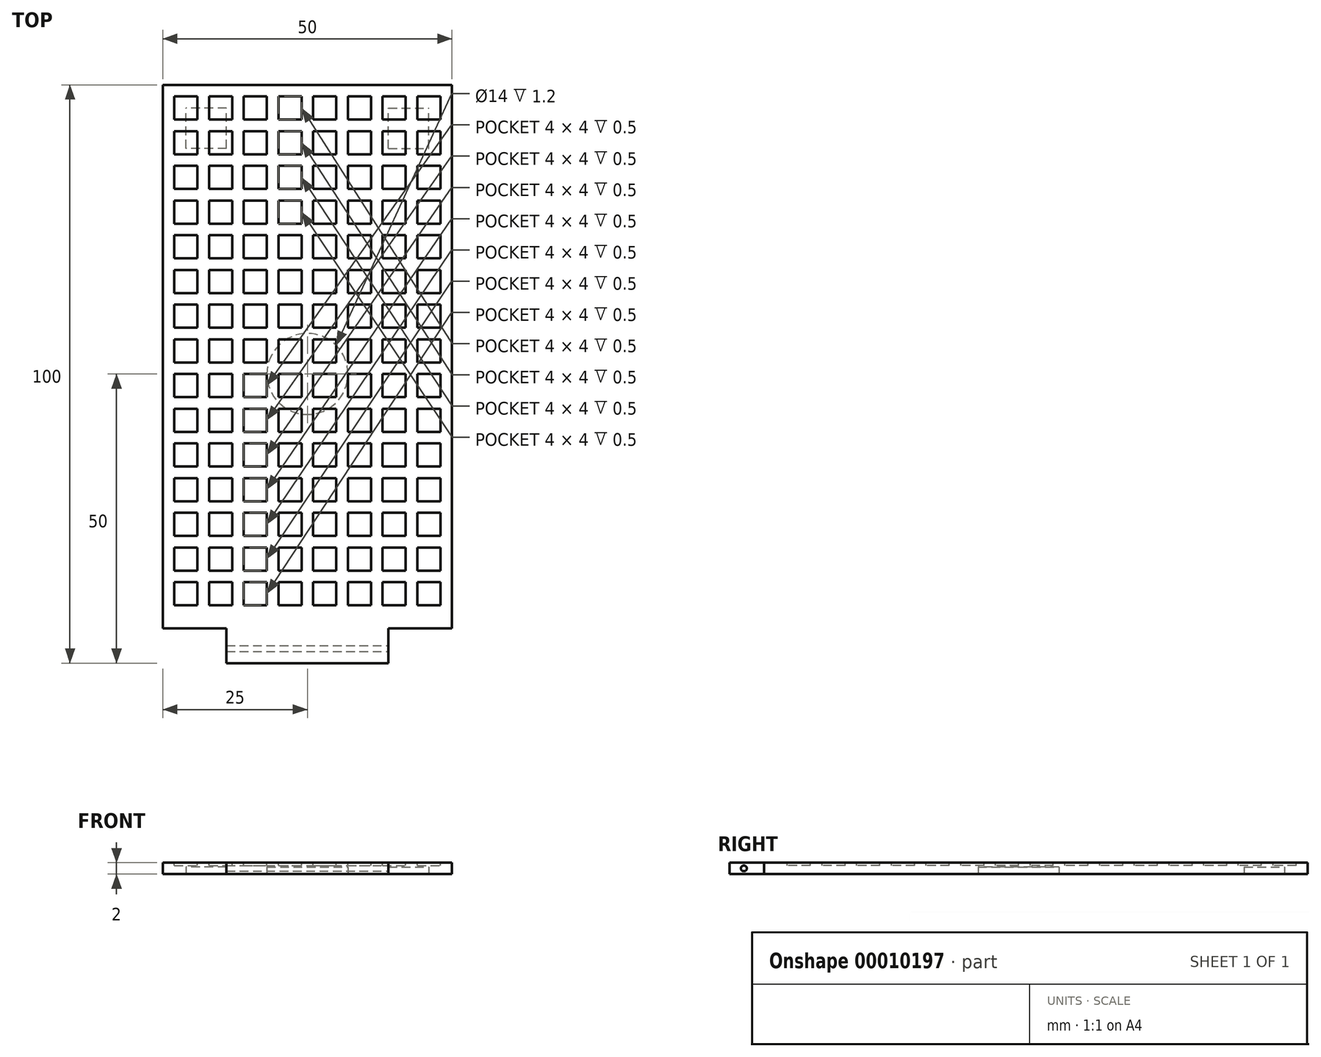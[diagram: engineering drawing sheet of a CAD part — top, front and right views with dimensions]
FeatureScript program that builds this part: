
annotation { "Feature Type Name" : "Feature", "Feature Type Description" : "" }
export const myFeature = defineFeature(function(context is Context, id is Id, definition is map)
    precondition{}
    {
        {
            var Q0;
            Q0=qCreatedBy(makeId("Top.planeOp"),FACE);
            var sketch = newSketch(context, id + "F0", { "sketchPlane" : qUnion([Q0])});
            skLineSegment(sketch, "E0.bottom", {"start": v(-28, -65.66) * mm, "end": v(0, -65.66) * mm});
            skLineSegment(sketch, "E0.top", {"start": v(-39, 34.34) * mm, "end": v(11, 34.34) * mm});
            skLineSegment(sketch, "E0.left", {"start": v(-39, -59.66) * mm, "end": v(-39, 34.34) * mm});
            skLineSegment(sketch, "E0.right", {"start": v(11, -59.66) * mm, "end": v(11, 34.34) * mm});
            skLineSegment(sketch, "E1.top", {"start": v(-39, -59.66) * mm, "end": v(-28, -59.66) * mm});
            skLineSegment(sketch, "E1.right", {"start": v(-28, -65.66) * mm, "end": v(-28, -59.66) * mm});
            skLineSegment(sketch, "E2.top", {"start": v(11, -59.66) * mm, "end": v(0, -59.66) * mm});
            skLineSegment(sketch, "E2.right", {"start": v(0, -65.66) * mm, "end": v(0, -59.66) * mm});
            skSolve(sketch);
        }
        {
            var Q0;
            Q0 = qSketchRegion(id + "F0", true);
            extrude(context, id + "F1", {"entities" : qUnion([Q0]), "depth" : 2 * mm});
        }
        {
            var Q0;
            Q0=makeQuery(id+"F1.opExtrude","CAP_FACE",FACE,{"disambiguationData":[OSD([sQuery(id+"F0.wireOp",EDGE,"E0.bottom"),sQuery(id+"F0.wireOp",EDGE,"E0.top"),sQuery(id+"F0.wireOp",EDGE,"E0.left"),sQuery(id+"F0.wireOp",EDGE,"E0.right"),sQuery(id+"F0.wireOp",EDGE,"E1.top"),sQuery(id+"F0.wireOp",EDGE,"E1.right"),sQuery(id+"F0.wireOp",EDGE,"E2.top"),sQuery(id+"F0.wireOp",EDGE,"E2.right")])],"isStart":false});
            var sketch = newSketch(context, id + "F2", { "sketchPlane" : qUnion([Q0])});
            skLineSegment(sketch, "E3.bottom", {"start": v(-37, 32.34) * mm, "end": v(-33, 32.34) * mm});
            skLineSegment(sketch, "E3.top", {"start": v(-37, 28.34) * mm, "end": v(-33, 28.34) * mm});
            skLineSegment(sketch, "E3.left", {"start": v(-37, 32.34) * mm, "end": v(-37, 28.34) * mm});
            skLineSegment(sketch, "E3.right", {"start": v(-33, 32.34) * mm, "end": v(-33, 28.34) * mm});
            skLineSegment(sketch, "E4.0.1.0", {"start": v(-37, 26.34) * mm, "end": v(-37, 22.34) * mm});
            skLineSegment(sketch, "E4.0.1.1", {"start": v(-33, 26.34) * mm, "end": v(-33, 22.34) * mm});
            skLineSegment(sketch, "E4.0.1.2", {"start": v(-37, 22.34) * mm, "end": v(-33, 22.34) * mm});
            skLineSegment(sketch, "E4.0.1.3", {"start": v(-37, 26.34) * mm, "end": v(-33, 26.34) * mm});
            skLineSegment(sketch, "E4.0.2.0", {"start": v(-37, 20.34) * mm, "end": v(-37, 16.34) * mm});
            skLineSegment(sketch, "E4.0.2.1", {"start": v(-33, 20.34) * mm, "end": v(-33, 16.34) * mm});
            skLineSegment(sketch, "E4.0.2.2", {"start": v(-37, 16.34) * mm, "end": v(-33, 16.34) * mm});
            skLineSegment(sketch, "E4.0.2.3", {"start": v(-37, 20.34) * mm, "end": v(-33, 20.34) * mm});
            skLineSegment(sketch, "E4.0.3.0", {"start": v(-37, 14.34) * mm, "end": v(-37, 10.34) * mm});
            skLineSegment(sketch, "E4.0.3.1", {"start": v(-33, 14.34) * mm, "end": v(-33, 10.34) * mm});
            skLineSegment(sketch, "E4.0.3.2", {"start": v(-37, 10.34) * mm, "end": v(-33, 10.34) * mm});
            skLineSegment(sketch, "E4.0.3.3", {"start": v(-37, 14.34) * mm, "end": v(-33, 14.34) * mm});
            skLineSegment(sketch, "E4.0.4.0", {"start": v(-37, 8.34) * mm, "end": v(-37, 4.34) * mm});
            skLineSegment(sketch, "E4.0.4.1", {"start": v(-33, 8.34) * mm, "end": v(-33, 4.34) * mm});
            skLineSegment(sketch, "E4.0.4.2", {"start": v(-37, 4.34) * mm, "end": v(-33, 4.34) * mm});
            skLineSegment(sketch, "E4.0.4.3", {"start": v(-37, 8.34) * mm, "end": v(-33, 8.34) * mm});
            skLineSegment(sketch, "E4.0.5.0", {"start": v(-37, 2.34) * mm, "end": v(-37, -1.66) * mm});
            skLineSegment(sketch, "E4.0.5.1", {"start": v(-33, 2.34) * mm, "end": v(-33, -1.66) * mm});
            skLineSegment(sketch, "E4.0.5.2", {"start": v(-37, -1.66) * mm, "end": v(-33, -1.66) * mm});
            skLineSegment(sketch, "E4.0.5.3", {"start": v(-37, 2.34) * mm, "end": v(-33, 2.34) * mm});
            skLineSegment(sketch, "E4.0.6.0", {"start": v(-37, -3.66) * mm, "end": v(-37, -7.66) * mm});
            skLineSegment(sketch, "E4.0.6.1", {"start": v(-33, -3.66) * mm, "end": v(-33, -7.66) * mm});
            skLineSegment(sketch, "E4.0.6.2", {"start": v(-37, -7.66) * mm, "end": v(-33, -7.66) * mm});
            skLineSegment(sketch, "E4.0.6.3", {"start": v(-37, -3.66) * mm, "end": v(-33, -3.66) * mm});
            skLineSegment(sketch, "E4.0.7.0", {"start": v(-37, -9.66) * mm, "end": v(-37, -13.66) * mm});
            skLineSegment(sketch, "E4.0.7.1", {"start": v(-33, -9.66) * mm, "end": v(-33, -13.66) * mm});
            skLineSegment(sketch, "E4.0.7.2", {"start": v(-37, -13.66) * mm, "end": v(-33, -13.66) * mm});
            skLineSegment(sketch, "E4.0.7.3", {"start": v(-37, -9.66) * mm, "end": v(-33, -9.66) * mm});
            skLineSegment(sketch, "E4.0.8.0", {"start": v(-37, -15.66) * mm, "end": v(-37, -19.66) * mm});
            skLineSegment(sketch, "E4.0.8.1", {"start": v(-33, -15.66) * mm, "end": v(-33, -19.66) * mm});
            skLineSegment(sketch, "E4.0.8.2", {"start": v(-37, -19.66) * mm, "end": v(-33, -19.66) * mm});
            skLineSegment(sketch, "E4.0.8.3", {"start": v(-37, -15.66) * mm, "end": v(-33, -15.66) * mm});
            skLineSegment(sketch, "E4.0.9.0", {"start": v(-37, -21.66) * mm, "end": v(-37, -25.66) * mm});
            skLineSegment(sketch, "E4.0.9.1", {"start": v(-33, -21.66) * mm, "end": v(-33, -25.66) * mm});
            skLineSegment(sketch, "E4.0.9.2", {"start": v(-37, -25.66) * mm, "end": v(-33, -25.66) * mm});
            skLineSegment(sketch, "E4.0.9.3", {"start": v(-37, -21.66) * mm, "end": v(-33, -21.66) * mm});
            skLineSegment(sketch, "E4.0.10.0", {"start": v(-37, -27.66) * mm, "end": v(-37, -31.66) * mm});
            skLineSegment(sketch, "E4.0.10.1", {"start": v(-33, -27.66) * mm, "end": v(-33, -31.66) * mm});
            skLineSegment(sketch, "E4.0.10.2", {"start": v(-37, -31.66) * mm, "end": v(-33, -31.66) * mm});
            skLineSegment(sketch, "E4.0.10.3", {"start": v(-37, -27.66) * mm, "end": v(-33, -27.66) * mm});
            skLineSegment(sketch, "E4.0.11.0", {"start": v(-37, -33.66) * mm, "end": v(-37, -37.66) * mm});
            skLineSegment(sketch, "E4.0.11.1", {"start": v(-33, -33.66) * mm, "end": v(-33, -37.66) * mm});
            skLineSegment(sketch, "E4.0.11.2", {"start": v(-37, -37.66) * mm, "end": v(-33, -37.66) * mm});
            skLineSegment(sketch, "E4.0.11.3", {"start": v(-37, -33.66) * mm, "end": v(-33, -33.66) * mm});
            skLineSegment(sketch, "E4.0.12.0", {"start": v(-37, -39.66) * mm, "end": v(-37, -43.66) * mm});
            skLineSegment(sketch, "E4.0.12.1", {"start": v(-33, -39.66) * mm, "end": v(-33, -43.66) * mm});
            skLineSegment(sketch, "E4.0.12.2", {"start": v(-37, -43.66) * mm, "end": v(-33, -43.66) * mm});
            skLineSegment(sketch, "E4.0.12.3", {"start": v(-37, -39.66) * mm, "end": v(-33, -39.66) * mm});
            skLineSegment(sketch, "E4.0.13.0", {"start": v(-37, -45.66) * mm, "end": v(-37, -49.66) * mm});
            skLineSegment(sketch, "E4.0.13.1", {"start": v(-33, -45.66) * mm, "end": v(-33, -49.66) * mm});
            skLineSegment(sketch, "E4.0.13.2", {"start": v(-37, -49.66) * mm, "end": v(-33, -49.66) * mm});
            skLineSegment(sketch, "E4.0.13.3", {"start": v(-37, -45.66) * mm, "end": v(-33, -45.66) * mm});
            skLineSegment(sketch, "E4.0.14.0", {"start": v(-37, -51.66) * mm, "end": v(-37, -55.66) * mm});
            skLineSegment(sketch, "E4.0.14.1", {"start": v(-33, -51.66) * mm, "end": v(-33, -55.66) * mm});
            skLineSegment(sketch, "E4.0.14.2", {"start": v(-37, -55.66) * mm, "end": v(-33, -55.66) * mm});
            skLineSegment(sketch, "E4.0.14.3", {"start": v(-37, -51.66) * mm, "end": v(-33, -51.66) * mm});
            skLineSegment(sketch, "E4.1.0.0", {"start": v(-31, 32.34) * mm, "end": v(-31, 28.34) * mm});
            skLineSegment(sketch, "E4.1.0.1", {"start": v(-27, 32.34) * mm, "end": v(-27, 28.34) * mm});
            skLineSegment(sketch, "E4.1.0.2", {"start": v(-31, 28.34) * mm, "end": v(-27, 28.34) * mm});
            skLineSegment(sketch, "E4.1.0.3", {"start": v(-31, 32.34) * mm, "end": v(-27, 32.34) * mm});
            skLineSegment(sketch, "E4.1.1.0", {"start": v(-31, 26.34) * mm, "end": v(-31, 22.34) * mm});
            skLineSegment(sketch, "E4.1.1.1", {"start": v(-27, 26.34) * mm, "end": v(-27, 22.34) * mm});
            skLineSegment(sketch, "E4.1.1.2", {"start": v(-31, 22.34) * mm, "end": v(-27, 22.34) * mm});
            skLineSegment(sketch, "E4.1.1.3", {"start": v(-31, 26.34) * mm, "end": v(-27, 26.34) * mm});
            skLineSegment(sketch, "E4.1.2.0", {"start": v(-31, 20.34) * mm, "end": v(-31, 16.34) * mm});
            skLineSegment(sketch, "E4.1.2.1", {"start": v(-27, 20.34) * mm, "end": v(-27, 16.34) * mm});
            skLineSegment(sketch, "E4.1.2.2", {"start": v(-31, 16.34) * mm, "end": v(-27, 16.34) * mm});
            skLineSegment(sketch, "E4.1.2.3", {"start": v(-31, 20.34) * mm, "end": v(-27, 20.34) * mm});
            skLineSegment(sketch, "E4.1.3.0", {"start": v(-31, 14.34) * mm, "end": v(-31, 10.34) * mm});
            skLineSegment(sketch, "E4.1.3.1", {"start": v(-27, 14.34) * mm, "end": v(-27, 10.34) * mm});
            skLineSegment(sketch, "E4.1.3.2", {"start": v(-31, 10.34) * mm, "end": v(-27, 10.34) * mm});
            skLineSegment(sketch, "E4.1.3.3", {"start": v(-31, 14.34) * mm, "end": v(-27, 14.34) * mm});
            skLineSegment(sketch, "E4.1.4.0", {"start": v(-31, 8.34) * mm, "end": v(-31, 4.34) * mm});
            skLineSegment(sketch, "E4.1.4.1", {"start": v(-27, 8.34) * mm, "end": v(-27, 4.34) * mm});
            skLineSegment(sketch, "E4.1.4.2", {"start": v(-31, 4.34) * mm, "end": v(-27, 4.34) * mm});
            skLineSegment(sketch, "E4.1.4.3", {"start": v(-31, 8.34) * mm, "end": v(-27, 8.34) * mm});
            skLineSegment(sketch, "E4.1.5.0", {"start": v(-31, 2.34) * mm, "end": v(-31, -1.66) * mm});
            skLineSegment(sketch, "E4.1.5.1", {"start": v(-27, 2.34) * mm, "end": v(-27, -1.66) * mm});
            skLineSegment(sketch, "E4.1.5.2", {"start": v(-31, -1.66) * mm, "end": v(-27, -1.66) * mm});
            skLineSegment(sketch, "E4.1.5.3", {"start": v(-31, 2.34) * mm, "end": v(-27, 2.34) * mm});
            skLineSegment(sketch, "E4.1.6.0", {"start": v(-31, -3.66) * mm, "end": v(-31, -7.66) * mm});
            skLineSegment(sketch, "E4.1.6.1", {"start": v(-27, -3.66) * mm, "end": v(-27, -7.66) * mm});
            skLineSegment(sketch, "E4.1.6.2", {"start": v(-31, -7.66) * mm, "end": v(-27, -7.66) * mm});
            skLineSegment(sketch, "E4.1.6.3", {"start": v(-31, -3.66) * mm, "end": v(-27, -3.66) * mm});
            skLineSegment(sketch, "E4.1.7.0", {"start": v(-31, -9.66) * mm, "end": v(-31, -13.66) * mm});
            skLineSegment(sketch, "E4.1.7.1", {"start": v(-27, -9.66) * mm, "end": v(-27, -13.66) * mm});
            skLineSegment(sketch, "E4.1.7.2", {"start": v(-31, -13.66) * mm, "end": v(-27, -13.66) * mm});
            skLineSegment(sketch, "E4.1.7.3", {"start": v(-31, -9.66) * mm, "end": v(-27, -9.66) * mm});
            skLineSegment(sketch, "E4.1.8.0", {"start": v(-31, -15.66) * mm, "end": v(-31, -19.66) * mm});
            skLineSegment(sketch, "E4.1.8.1", {"start": v(-27, -15.66) * mm, "end": v(-27, -19.66) * mm});
            skLineSegment(sketch, "E4.1.8.2", {"start": v(-31, -19.66) * mm, "end": v(-27, -19.66) * mm});
            skLineSegment(sketch, "E4.1.8.3", {"start": v(-31, -15.66) * mm, "end": v(-27, -15.66) * mm});
            skLineSegment(sketch, "E4.1.9.0", {"start": v(-31, -21.66) * mm, "end": v(-31, -25.66) * mm});
            skLineSegment(sketch, "E4.1.9.1", {"start": v(-27, -21.66) * mm, "end": v(-27, -25.66) * mm});
            skLineSegment(sketch, "E4.1.9.2", {"start": v(-31, -25.66) * mm, "end": v(-27, -25.66) * mm});
            skLineSegment(sketch, "E4.1.9.3", {"start": v(-31, -21.66) * mm, "end": v(-27, -21.66) * mm});
            skLineSegment(sketch, "E4.1.10.0", {"start": v(-31, -27.66) * mm, "end": v(-31, -31.66) * mm});
            skLineSegment(sketch, "E4.1.10.1", {"start": v(-27, -27.66) * mm, "end": v(-27, -31.66) * mm});
            skLineSegment(sketch, "E4.1.10.2", {"start": v(-31, -31.66) * mm, "end": v(-27, -31.66) * mm});
            skLineSegment(sketch, "E4.1.10.3", {"start": v(-31, -27.66) * mm, "end": v(-27, -27.66) * mm});
            skLineSegment(sketch, "E4.1.11.0", {"start": v(-31, -33.66) * mm, "end": v(-31, -37.66) * mm});
            skLineSegment(sketch, "E4.1.11.1", {"start": v(-27, -33.66) * mm, "end": v(-27, -37.66) * mm});
            skLineSegment(sketch, "E4.1.11.2", {"start": v(-31, -37.66) * mm, "end": v(-27, -37.66) * mm});
            skLineSegment(sketch, "E4.1.11.3", {"start": v(-31, -33.66) * mm, "end": v(-27, -33.66) * mm});
            skLineSegment(sketch, "E4.1.12.0", {"start": v(-31, -39.66) * mm, "end": v(-31, -43.66) * mm});
            skLineSegment(sketch, "E4.1.12.1", {"start": v(-27, -39.66) * mm, "end": v(-27, -43.66) * mm});
            skLineSegment(sketch, "E4.1.12.2", {"start": v(-31, -43.66) * mm, "end": v(-27, -43.66) * mm});
            skLineSegment(sketch, "E4.1.12.3", {"start": v(-31, -39.66) * mm, "end": v(-27, -39.66) * mm});
            skLineSegment(sketch, "E4.1.13.0", {"start": v(-31, -45.66) * mm, "end": v(-31, -49.66) * mm});
            skLineSegment(sketch, "E4.1.13.1", {"start": v(-27, -45.66) * mm, "end": v(-27, -49.66) * mm});
            skLineSegment(sketch, "E4.1.13.2", {"start": v(-31, -49.66) * mm, "end": v(-27, -49.66) * mm});
            skLineSegment(sketch, "E4.1.13.3", {"start": v(-31, -45.66) * mm, "end": v(-27, -45.66) * mm});
            skLineSegment(sketch, "E4.1.14.0", {"start": v(-31, -51.66) * mm, "end": v(-31, -55.66) * mm});
            skLineSegment(sketch, "E4.1.14.1", {"start": v(-27, -51.66) * mm, "end": v(-27, -55.66) * mm});
            skLineSegment(sketch, "E4.1.14.2", {"start": v(-31, -55.66) * mm, "end": v(-27, -55.66) * mm});
            skLineSegment(sketch, "E4.1.14.3", {"start": v(-31, -51.66) * mm, "end": v(-27, -51.66) * mm});
            skLineSegment(sketch, "E4.2.0.0", {"start": v(-25, 32.34) * mm, "end": v(-25, 28.34) * mm});
            skLineSegment(sketch, "E4.2.0.1", {"start": v(-21, 32.34) * mm, "end": v(-21, 28.34) * mm});
            skLineSegment(sketch, "E4.2.0.2", {"start": v(-25, 28.34) * mm, "end": v(-21, 28.34) * mm});
            skLineSegment(sketch, "E4.2.0.3", {"start": v(-25, 32.34) * mm, "end": v(-21, 32.34) * mm});
            skLineSegment(sketch, "E4.2.1.0", {"start": v(-25, 26.34) * mm, "end": v(-25, 22.34) * mm});
            skLineSegment(sketch, "E4.2.1.1", {"start": v(-21, 26.34) * mm, "end": v(-21, 22.34) * mm});
            skLineSegment(sketch, "E4.2.1.2", {"start": v(-25, 22.34) * mm, "end": v(-21, 22.34) * mm});
            skLineSegment(sketch, "E4.2.1.3", {"start": v(-25, 26.34) * mm, "end": v(-21, 26.34) * mm});
            skLineSegment(sketch, "E4.2.2.0", {"start": v(-25, 20.34) * mm, "end": v(-25, 16.34) * mm});
            skLineSegment(sketch, "E4.2.2.1", {"start": v(-21, 20.34) * mm, "end": v(-21, 16.34) * mm});
            skLineSegment(sketch, "E4.2.2.2", {"start": v(-25, 16.34) * mm, "end": v(-21, 16.34) * mm});
            skLineSegment(sketch, "E4.2.2.3", {"start": v(-25, 20.34) * mm, "end": v(-21, 20.34) * mm});
            skLineSegment(sketch, "E4.2.3.0", {"start": v(-25, 14.34) * mm, "end": v(-25, 10.34) * mm});
            skLineSegment(sketch, "E4.2.3.1", {"start": v(-21, 14.34) * mm, "end": v(-21, 10.34) * mm});
            skLineSegment(sketch, "E4.2.3.2", {"start": v(-25, 10.34) * mm, "end": v(-21, 10.34) * mm});
            skLineSegment(sketch, "E4.2.3.3", {"start": v(-25, 14.34) * mm, "end": v(-21, 14.34) * mm});
            skLineSegment(sketch, "E4.2.4.0", {"start": v(-25, 8.34) * mm, "end": v(-25, 4.34) * mm});
            skLineSegment(sketch, "E4.2.4.1", {"start": v(-21, 8.34) * mm, "end": v(-21, 4.34) * mm});
            skLineSegment(sketch, "E4.2.4.2", {"start": v(-25, 4.34) * mm, "end": v(-21, 4.34) * mm});
            skLineSegment(sketch, "E4.2.4.3", {"start": v(-25, 8.34) * mm, "end": v(-21, 8.34) * mm});
            skLineSegment(sketch, "E4.2.5.0", {"start": v(-25, 2.34) * mm, "end": v(-25, -1.66) * mm});
            skLineSegment(sketch, "E4.2.5.1", {"start": v(-21, 2.34) * mm, "end": v(-21, -1.66) * mm});
            skLineSegment(sketch, "E4.2.5.2", {"start": v(-25, -1.66) * mm, "end": v(-21, -1.66) * mm});
            skLineSegment(sketch, "E4.2.5.3", {"start": v(-25, 2.34) * mm, "end": v(-21, 2.34) * mm});
            skLineSegment(sketch, "E4.2.6.0", {"start": v(-25, -3.66) * mm, "end": v(-25, -7.66) * mm});
            skLineSegment(sketch, "E4.2.6.1", {"start": v(-21, -3.66) * mm, "end": v(-21, -7.66) * mm});
            skLineSegment(sketch, "E4.2.6.2", {"start": v(-25, -7.66) * mm, "end": v(-21, -7.66) * mm});
            skLineSegment(sketch, "E4.2.6.3", {"start": v(-25, -3.66) * mm, "end": v(-21, -3.66) * mm});
            skLineSegment(sketch, "E4.2.7.0", {"start": v(-25, -9.66) * mm, "end": v(-25, -13.66) * mm});
            skLineSegment(sketch, "E4.2.7.1", {"start": v(-21, -9.66) * mm, "end": v(-21, -13.66) * mm});
            skLineSegment(sketch, "E4.2.7.2", {"start": v(-25, -13.66) * mm, "end": v(-21, -13.66) * mm});
            skLineSegment(sketch, "E4.2.7.3", {"start": v(-25, -9.66) * mm, "end": v(-21, -9.66) * mm});
            skLineSegment(sketch, "E4.2.8.0", {"start": v(-25, -15.66) * mm, "end": v(-25, -19.66) * mm});
            skLineSegment(sketch, "E4.2.8.1", {"start": v(-21, -15.66) * mm, "end": v(-21, -19.66) * mm});
            skLineSegment(sketch, "E4.2.8.2", {"start": v(-25, -19.66) * mm, "end": v(-21, -19.66) * mm});
            skLineSegment(sketch, "E4.2.8.3", {"start": v(-25, -15.66) * mm, "end": v(-21, -15.66) * mm});
            skLineSegment(sketch, "E4.2.9.0", {"start": v(-25, -21.66) * mm, "end": v(-25, -25.66) * mm});
            skLineSegment(sketch, "E4.2.9.1", {"start": v(-21, -21.66) * mm, "end": v(-21, -25.66) * mm});
            skLineSegment(sketch, "E4.2.9.2", {"start": v(-25, -25.66) * mm, "end": v(-21, -25.66) * mm});
            skLineSegment(sketch, "E4.2.9.3", {"start": v(-25, -21.66) * mm, "end": v(-21, -21.66) * mm});
            skLineSegment(sketch, "E4.2.10.0", {"start": v(-25, -27.66) * mm, "end": v(-25, -31.66) * mm});
            skLineSegment(sketch, "E4.2.10.1", {"start": v(-21, -27.66) * mm, "end": v(-21, -31.66) * mm});
            skLineSegment(sketch, "E4.2.10.2", {"start": v(-25, -31.66) * mm, "end": v(-21, -31.66) * mm});
            skLineSegment(sketch, "E4.2.10.3", {"start": v(-25, -27.66) * mm, "end": v(-21, -27.66) * mm});
            skLineSegment(sketch, "E4.2.11.0", {"start": v(-25, -33.66) * mm, "end": v(-25, -37.66) * mm});
            skLineSegment(sketch, "E4.2.11.1", {"start": v(-21, -33.66) * mm, "end": v(-21, -37.66) * mm});
            skLineSegment(sketch, "E4.2.11.2", {"start": v(-25, -37.66) * mm, "end": v(-21, -37.66) * mm});
            skLineSegment(sketch, "E4.2.11.3", {"start": v(-25, -33.66) * mm, "end": v(-21, -33.66) * mm});
            skLineSegment(sketch, "E4.2.12.0", {"start": v(-25, -39.66) * mm, "end": v(-25, -43.66) * mm});
            skLineSegment(sketch, "E4.2.12.1", {"start": v(-21, -39.66) * mm, "end": v(-21, -43.66) * mm});
            skLineSegment(sketch, "E4.2.12.2", {"start": v(-25, -43.66) * mm, "end": v(-21, -43.66) * mm});
            skLineSegment(sketch, "E4.2.12.3", {"start": v(-25, -39.66) * mm, "end": v(-21, -39.66) * mm});
            skLineSegment(sketch, "E4.2.13.0", {"start": v(-25, -45.66) * mm, "end": v(-25, -49.66) * mm});
            skLineSegment(sketch, "E4.2.13.1", {"start": v(-21, -45.66) * mm, "end": v(-21, -49.66) * mm});
            skLineSegment(sketch, "E4.2.13.2", {"start": v(-25, -49.66) * mm, "end": v(-21, -49.66) * mm});
            skLineSegment(sketch, "E4.2.13.3", {"start": v(-25, -45.66) * mm, "end": v(-21, -45.66) * mm});
            skLineSegment(sketch, "E4.2.14.0", {"start": v(-25, -51.66) * mm, "end": v(-25, -55.66) * mm});
            skLineSegment(sketch, "E4.2.14.1", {"start": v(-21, -51.66) * mm, "end": v(-21, -55.66) * mm});
            skLineSegment(sketch, "E4.2.14.2", {"start": v(-25, -55.66) * mm, "end": v(-21, -55.66) * mm});
            skLineSegment(sketch, "E4.2.14.3", {"start": v(-25, -51.66) * mm, "end": v(-21, -51.66) * mm});
            skLineSegment(sketch, "E4.3.0.0", {"start": v(-19, 32.34) * mm, "end": v(-19, 28.34) * mm});
            skLineSegment(sketch, "E4.3.0.1", {"start": v(-15, 32.34) * mm, "end": v(-15, 28.34) * mm});
            skLineSegment(sketch, "E4.3.0.2", {"start": v(-19, 28.34) * mm, "end": v(-15, 28.34) * mm});
            skLineSegment(sketch, "E4.3.0.3", {"start": v(-19, 32.34) * mm, "end": v(-15, 32.34) * mm});
            skLineSegment(sketch, "E4.3.1.0", {"start": v(-19, 26.34) * mm, "end": v(-19, 22.34) * mm});
            skLineSegment(sketch, "E4.3.1.1", {"start": v(-15, 26.34) * mm, "end": v(-15, 22.34) * mm});
            skLineSegment(sketch, "E4.3.1.2", {"start": v(-19, 22.34) * mm, "end": v(-15, 22.34) * mm});
            skLineSegment(sketch, "E4.3.1.3", {"start": v(-19, 26.34) * mm, "end": v(-15, 26.34) * mm});
            skLineSegment(sketch, "E4.3.2.0", {"start": v(-19, 20.34) * mm, "end": v(-19, 16.34) * mm});
            skLineSegment(sketch, "E4.3.2.1", {"start": v(-15, 20.34) * mm, "end": v(-15, 16.34) * mm});
            skLineSegment(sketch, "E4.3.2.2", {"start": v(-19, 16.34) * mm, "end": v(-15, 16.34) * mm});
            skLineSegment(sketch, "E4.3.2.3", {"start": v(-19, 20.34) * mm, "end": v(-15, 20.34) * mm});
            skLineSegment(sketch, "E4.3.3.0", {"start": v(-19, 14.34) * mm, "end": v(-19, 10.34) * mm});
            skLineSegment(sketch, "E4.3.3.1", {"start": v(-15, 14.34) * mm, "end": v(-15, 10.34) * mm});
            skLineSegment(sketch, "E4.3.3.2", {"start": v(-19, 10.34) * mm, "end": v(-15, 10.34) * mm});
            skLineSegment(sketch, "E4.3.3.3", {"start": v(-19, 14.34) * mm, "end": v(-15, 14.34) * mm});
            skLineSegment(sketch, "E4.3.4.0", {"start": v(-19, 8.34) * mm, "end": v(-19, 4.34) * mm});
            skLineSegment(sketch, "E4.3.4.1", {"start": v(-15, 8.34) * mm, "end": v(-15, 4.34) * mm});
            skLineSegment(sketch, "E4.3.4.2", {"start": v(-19, 4.34) * mm, "end": v(-15, 4.34) * mm});
            skLineSegment(sketch, "E4.3.4.3", {"start": v(-19, 8.34) * mm, "end": v(-15, 8.34) * mm});
            skLineSegment(sketch, "E4.3.5.0", {"start": v(-19, 2.34) * mm, "end": v(-19, -1.66) * mm});
            skLineSegment(sketch, "E4.3.5.1", {"start": v(-15, 2.34) * mm, "end": v(-15, -1.66) * mm});
            skLineSegment(sketch, "E4.3.5.2", {"start": v(-19, -1.66) * mm, "end": v(-15, -1.66) * mm});
            skLineSegment(sketch, "E4.3.5.3", {"start": v(-19, 2.34) * mm, "end": v(-15, 2.34) * mm});
            skLineSegment(sketch, "E4.3.6.0", {"start": v(-19, -3.66) * mm, "end": v(-19, -7.66) * mm});
            skLineSegment(sketch, "E4.3.6.1", {"start": v(-15, -3.66) * mm, "end": v(-15, -7.66) * mm});
            skLineSegment(sketch, "E4.3.6.2", {"start": v(-19, -7.66) * mm, "end": v(-15, -7.66) * mm});
            skLineSegment(sketch, "E4.3.6.3", {"start": v(-19, -3.66) * mm, "end": v(-15, -3.66) * mm});
            skLineSegment(sketch, "E4.3.7.0", {"start": v(-19, -9.66) * mm, "end": v(-19, -13.66) * mm});
            skLineSegment(sketch, "E4.3.7.1", {"start": v(-15, -9.66) * mm, "end": v(-15, -13.66) * mm});
            skLineSegment(sketch, "E4.3.7.2", {"start": v(-19, -13.66) * mm, "end": v(-15, -13.66) * mm});
            skLineSegment(sketch, "E4.3.7.3", {"start": v(-19, -9.66) * mm, "end": v(-15, -9.66) * mm});
            skLineSegment(sketch, "E4.3.8.0", {"start": v(-19, -15.66) * mm, "end": v(-19, -19.66) * mm});
            skLineSegment(sketch, "E4.3.8.1", {"start": v(-15, -15.66) * mm, "end": v(-15, -19.66) * mm});
            skLineSegment(sketch, "E4.3.8.2", {"start": v(-19, -19.66) * mm, "end": v(-15, -19.66) * mm});
            skLineSegment(sketch, "E4.3.8.3", {"start": v(-19, -15.66) * mm, "end": v(-15, -15.66) * mm});
            skLineSegment(sketch, "E4.3.9.0", {"start": v(-19, -21.66) * mm, "end": v(-19, -25.66) * mm});
            skLineSegment(sketch, "E4.3.9.1", {"start": v(-15, -21.66) * mm, "end": v(-15, -25.66) * mm});
            skLineSegment(sketch, "E4.3.9.2", {"start": v(-19, -25.66) * mm, "end": v(-15, -25.66) * mm});
            skLineSegment(sketch, "E4.3.9.3", {"start": v(-19, -21.66) * mm, "end": v(-15, -21.66) * mm});
            skLineSegment(sketch, "E4.3.10.0", {"start": v(-19, -27.66) * mm, "end": v(-19, -31.66) * mm});
            skLineSegment(sketch, "E4.3.10.1", {"start": v(-15, -27.66) * mm, "end": v(-15, -31.66) * mm});
            skLineSegment(sketch, "E4.3.10.2", {"start": v(-19, -31.66) * mm, "end": v(-15, -31.66) * mm});
            skLineSegment(sketch, "E4.3.10.3", {"start": v(-19, -27.66) * mm, "end": v(-15, -27.66) * mm});
            skLineSegment(sketch, "E4.3.11.0", {"start": v(-19, -33.66) * mm, "end": v(-19, -37.66) * mm});
            skLineSegment(sketch, "E4.3.11.1", {"start": v(-15, -33.66) * mm, "end": v(-15, -37.66) * mm});
            skLineSegment(sketch, "E4.3.11.2", {"start": v(-19, -37.66) * mm, "end": v(-15, -37.66) * mm});
            skLineSegment(sketch, "E4.3.11.3", {"start": v(-19, -33.66) * mm, "end": v(-15, -33.66) * mm});
            skLineSegment(sketch, "E4.3.12.0", {"start": v(-19, -39.66) * mm, "end": v(-19, -43.66) * mm});
            skLineSegment(sketch, "E4.3.12.1", {"start": v(-15, -39.66) * mm, "end": v(-15, -43.66) * mm});
            skLineSegment(sketch, "E4.3.12.2", {"start": v(-19, -43.66) * mm, "end": v(-15, -43.66) * mm});
            skLineSegment(sketch, "E4.3.12.3", {"start": v(-19, -39.66) * mm, "end": v(-15, -39.66) * mm});
            skLineSegment(sketch, "E4.3.13.0", {"start": v(-19, -45.66) * mm, "end": v(-19, -49.66) * mm});
            skLineSegment(sketch, "E4.3.13.1", {"start": v(-15, -45.66) * mm, "end": v(-15, -49.66) * mm});
            skLineSegment(sketch, "E4.3.13.2", {"start": v(-19, -49.66) * mm, "end": v(-15, -49.66) * mm});
            skLineSegment(sketch, "E4.3.13.3", {"start": v(-19, -45.66) * mm, "end": v(-15, -45.66) * mm});
            skLineSegment(sketch, "E4.3.14.0", {"start": v(-19, -51.66) * mm, "end": v(-19, -55.66) * mm});
            skLineSegment(sketch, "E4.3.14.1", {"start": v(-15, -51.66) * mm, "end": v(-15, -55.66) * mm});
            skLineSegment(sketch, "E4.3.14.2", {"start": v(-19, -55.66) * mm, "end": v(-15, -55.66) * mm});
            skLineSegment(sketch, "E4.3.14.3", {"start": v(-19, -51.66) * mm, "end": v(-15, -51.66) * mm});
            skLineSegment(sketch, "E4.4.0.0", {"start": v(-13, 32.34) * mm, "end": v(-13, 28.34) * mm});
            skLineSegment(sketch, "E4.4.0.1", {"start": v(-9, 32.34) * mm, "end": v(-9, 28.34) * mm});
            skLineSegment(sketch, "E4.4.0.2", {"start": v(-13, 28.34) * mm, "end": v(-9, 28.34) * mm});
            skLineSegment(sketch, "E4.4.0.3", {"start": v(-13, 32.34) * mm, "end": v(-9, 32.34) * mm});
            skLineSegment(sketch, "E4.4.1.0", {"start": v(-13, 26.34) * mm, "end": v(-13, 22.34) * mm});
            skLineSegment(sketch, "E4.4.1.1", {"start": v(-9, 26.34) * mm, "end": v(-9, 22.34) * mm});
            skLineSegment(sketch, "E4.4.1.2", {"start": v(-13, 22.34) * mm, "end": v(-9, 22.34) * mm});
            skLineSegment(sketch, "E4.4.1.3", {"start": v(-13, 26.34) * mm, "end": v(-9, 26.34) * mm});
            skLineSegment(sketch, "E4.4.2.0", {"start": v(-13, 20.34) * mm, "end": v(-13, 16.34) * mm});
            skLineSegment(sketch, "E4.4.2.1", {"start": v(-9, 20.34) * mm, "end": v(-9, 16.34) * mm});
            skLineSegment(sketch, "E4.4.2.2", {"start": v(-13, 16.34) * mm, "end": v(-9, 16.34) * mm});
            skLineSegment(sketch, "E4.4.2.3", {"start": v(-13, 20.34) * mm, "end": v(-9, 20.34) * mm});
            skLineSegment(sketch, "E4.4.3.0", {"start": v(-13, 14.34) * mm, "end": v(-13, 10.34) * mm});
            skLineSegment(sketch, "E4.4.3.1", {"start": v(-9, 14.34) * mm, "end": v(-9, 10.34) * mm});
            skLineSegment(sketch, "E4.4.3.2", {"start": v(-13, 10.34) * mm, "end": v(-9, 10.34) * mm});
            skLineSegment(sketch, "E4.4.3.3", {"start": v(-13, 14.34) * mm, "end": v(-9, 14.34) * mm});
            skLineSegment(sketch, "E4.4.4.0", {"start": v(-13, 8.34) * mm, "end": v(-13, 4.34) * mm});
            skLineSegment(sketch, "E4.4.4.1", {"start": v(-9, 8.34) * mm, "end": v(-9, 4.34) * mm});
            skLineSegment(sketch, "E4.4.4.2", {"start": v(-13, 4.34) * mm, "end": v(-9, 4.34) * mm});
            skLineSegment(sketch, "E4.4.4.3", {"start": v(-13, 8.34) * mm, "end": v(-9, 8.34) * mm});
            skLineSegment(sketch, "E4.4.5.0", {"start": v(-13, 2.34) * mm, "end": v(-13, -1.66) * mm});
            skLineSegment(sketch, "E4.4.5.1", {"start": v(-9, 2.34) * mm, "end": v(-9, -1.66) * mm});
            skLineSegment(sketch, "E4.4.5.2", {"start": v(-13, -1.66) * mm, "end": v(-9, -1.66) * mm});
            skLineSegment(sketch, "E4.4.5.3", {"start": v(-13, 2.34) * mm, "end": v(-9, 2.34) * mm});
            skLineSegment(sketch, "E4.4.6.0", {"start": v(-13, -3.66) * mm, "end": v(-13, -7.66) * mm});
            skLineSegment(sketch, "E4.4.6.1", {"start": v(-9, -3.66) * mm, "end": v(-9, -7.66) * mm});
            skLineSegment(sketch, "E4.4.6.2", {"start": v(-13, -7.66) * mm, "end": v(-9, -7.66) * mm});
            skLineSegment(sketch, "E4.4.6.3", {"start": v(-13, -3.66) * mm, "end": v(-9, -3.66) * mm});
            skLineSegment(sketch, "E4.4.7.0", {"start": v(-13, -9.66) * mm, "end": v(-13, -13.66) * mm});
            skLineSegment(sketch, "E4.4.7.1", {"start": v(-9, -9.66) * mm, "end": v(-9, -13.66) * mm});
            skLineSegment(sketch, "E4.4.7.2", {"start": v(-13, -13.66) * mm, "end": v(-9, -13.66) * mm});
            skLineSegment(sketch, "E4.4.7.3", {"start": v(-13, -9.66) * mm, "end": v(-9, -9.66) * mm});
            skLineSegment(sketch, "E4.4.8.0", {"start": v(-13, -15.66) * mm, "end": v(-13, -19.66) * mm});
            skLineSegment(sketch, "E4.4.8.1", {"start": v(-9, -15.66) * mm, "end": v(-9, -19.66) * mm});
            skLineSegment(sketch, "E4.4.8.2", {"start": v(-13, -19.66) * mm, "end": v(-9, -19.66) * mm});
            skLineSegment(sketch, "E4.4.8.3", {"start": v(-13, -15.66) * mm, "end": v(-9, -15.66) * mm});
            skLineSegment(sketch, "E4.4.9.0", {"start": v(-13, -21.66) * mm, "end": v(-13, -25.66) * mm});
            skLineSegment(sketch, "E4.4.9.1", {"start": v(-9, -21.66) * mm, "end": v(-9, -25.66) * mm});
            skLineSegment(sketch, "E4.4.9.2", {"start": v(-13, -25.66) * mm, "end": v(-9, -25.66) * mm});
            skLineSegment(sketch, "E4.4.9.3", {"start": v(-13, -21.66) * mm, "end": v(-9, -21.66) * mm});
            skLineSegment(sketch, "E4.4.10.0", {"start": v(-13, -27.66) * mm, "end": v(-13, -31.66) * mm});
            skLineSegment(sketch, "E4.4.10.1", {"start": v(-9, -27.66) * mm, "end": v(-9, -31.66) * mm});
            skLineSegment(sketch, "E4.4.10.2", {"start": v(-13, -31.66) * mm, "end": v(-9, -31.66) * mm});
            skLineSegment(sketch, "E4.4.10.3", {"start": v(-13, -27.66) * mm, "end": v(-9, -27.66) * mm});
            skLineSegment(sketch, "E4.4.11.0", {"start": v(-13, -33.66) * mm, "end": v(-13, -37.66) * mm});
            skLineSegment(sketch, "E4.4.11.1", {"start": v(-9, -33.66) * mm, "end": v(-9, -37.66) * mm});
            skLineSegment(sketch, "E4.4.11.2", {"start": v(-13, -37.66) * mm, "end": v(-9, -37.66) * mm});
            skLineSegment(sketch, "E4.4.11.3", {"start": v(-13, -33.66) * mm, "end": v(-9, -33.66) * mm});
            skLineSegment(sketch, "E4.4.12.0", {"start": v(-13, -39.66) * mm, "end": v(-13, -43.66) * mm});
            skLineSegment(sketch, "E4.4.12.1", {"start": v(-9, -39.66) * mm, "end": v(-9, -43.66) * mm});
            skLineSegment(sketch, "E4.4.12.2", {"start": v(-13, -43.66) * mm, "end": v(-9, -43.66) * mm});
            skLineSegment(sketch, "E4.4.12.3", {"start": v(-13, -39.66) * mm, "end": v(-9, -39.66) * mm});
            skLineSegment(sketch, "E4.4.13.0", {"start": v(-13, -45.66) * mm, "end": v(-13, -49.66) * mm});
            skLineSegment(sketch, "E4.4.13.1", {"start": v(-9, -45.66) * mm, "end": v(-9, -49.66) * mm});
            skLineSegment(sketch, "E4.4.13.2", {"start": v(-13, -49.66) * mm, "end": v(-9, -49.66) * mm});
            skLineSegment(sketch, "E4.4.13.3", {"start": v(-13, -45.66) * mm, "end": v(-9, -45.66) * mm});
            skLineSegment(sketch, "E4.4.14.0", {"start": v(-13, -51.66) * mm, "end": v(-13, -55.66) * mm});
            skLineSegment(sketch, "E4.4.14.1", {"start": v(-9, -51.66) * mm, "end": v(-9, -55.66) * mm});
            skLineSegment(sketch, "E4.4.14.2", {"start": v(-13, -55.66) * mm, "end": v(-9, -55.66) * mm});
            skLineSegment(sketch, "E4.4.14.3", {"start": v(-13, -51.66) * mm, "end": v(-9, -51.66) * mm});
            skLineSegment(sketch, "E4.5.0.0", {"start": v(-7, 32.34) * mm, "end": v(-7, 28.34) * mm});
            skLineSegment(sketch, "E4.5.0.1", {"start": v(-3, 32.34) * mm, "end": v(-3, 28.34) * mm});
            skLineSegment(sketch, "E4.5.0.2", {"start": v(-7, 28.34) * mm, "end": v(-3, 28.34) * mm});
            skLineSegment(sketch, "E4.5.0.3", {"start": v(-7, 32.34) * mm, "end": v(-3, 32.34) * mm});
            skLineSegment(sketch, "E4.5.1.0", {"start": v(-7, 26.34) * mm, "end": v(-7, 22.34) * mm});
            skLineSegment(sketch, "E4.5.1.1", {"start": v(-3, 26.34) * mm, "end": v(-3, 22.34) * mm});
            skLineSegment(sketch, "E4.5.1.2", {"start": v(-7, 22.34) * mm, "end": v(-3, 22.34) * mm});
            skLineSegment(sketch, "E4.5.1.3", {"start": v(-7, 26.34) * mm, "end": v(-3, 26.34) * mm});
            skLineSegment(sketch, "E4.5.2.0", {"start": v(-7, 20.34) * mm, "end": v(-7, 16.34) * mm});
            skLineSegment(sketch, "E4.5.2.1", {"start": v(-3, 20.34) * mm, "end": v(-3, 16.34) * mm});
            skLineSegment(sketch, "E4.5.2.2", {"start": v(-7, 16.34) * mm, "end": v(-3, 16.34) * mm});
            skLineSegment(sketch, "E4.5.2.3", {"start": v(-7, 20.34) * mm, "end": v(-3, 20.34) * mm});
            skLineSegment(sketch, "E4.5.3.0", {"start": v(-7, 14.34) * mm, "end": v(-7, 10.34) * mm});
            skLineSegment(sketch, "E4.5.3.1", {"start": v(-3, 14.34) * mm, "end": v(-3, 10.34) * mm});
            skLineSegment(sketch, "E4.5.3.2", {"start": v(-7, 10.34) * mm, "end": v(-3, 10.34) * mm});
            skLineSegment(sketch, "E4.5.3.3", {"start": v(-7, 14.34) * mm, "end": v(-3, 14.34) * mm});
            skLineSegment(sketch, "E4.5.4.0", {"start": v(-7, 8.34) * mm, "end": v(-7, 4.34) * mm});
            skLineSegment(sketch, "E4.5.4.1", {"start": v(-3, 8.34) * mm, "end": v(-3, 4.34) * mm});
            skLineSegment(sketch, "E4.5.4.2", {"start": v(-7, 4.34) * mm, "end": v(-3, 4.34) * mm});
            skLineSegment(sketch, "E4.5.4.3", {"start": v(-7, 8.34) * mm, "end": v(-3, 8.34) * mm});
            skLineSegment(sketch, "E4.5.5.0", {"start": v(-7, 2.34) * mm, "end": v(-7, -1.66) * mm});
            skLineSegment(sketch, "E4.5.5.1", {"start": v(-3, 2.34) * mm, "end": v(-3, -1.66) * mm});
            skLineSegment(sketch, "E4.5.5.2", {"start": v(-7, -1.66) * mm, "end": v(-3, -1.66) * mm});
            skLineSegment(sketch, "E4.5.5.3", {"start": v(-7, 2.34) * mm, "end": v(-3, 2.34) * mm});
            skLineSegment(sketch, "E4.5.6.0", {"start": v(-7, -3.66) * mm, "end": v(-7, -7.66) * mm});
            skLineSegment(sketch, "E4.5.6.1", {"start": v(-3, -3.66) * mm, "end": v(-3, -7.66) * mm});
            skLineSegment(sketch, "E4.5.6.2", {"start": v(-7, -7.66) * mm, "end": v(-3, -7.66) * mm});
            skLineSegment(sketch, "E4.5.6.3", {"start": v(-7, -3.66) * mm, "end": v(-3, -3.66) * mm});
            skLineSegment(sketch, "E4.5.7.0", {"start": v(-7, -9.66) * mm, "end": v(-7, -13.66) * mm});
            skLineSegment(sketch, "E4.5.7.1", {"start": v(-3, -9.66) * mm, "end": v(-3, -13.66) * mm});
            skLineSegment(sketch, "E4.5.7.2", {"start": v(-7, -13.66) * mm, "end": v(-3, -13.66) * mm});
            skLineSegment(sketch, "E4.5.7.3", {"start": v(-7, -9.66) * mm, "end": v(-3, -9.66) * mm});
            skLineSegment(sketch, "E4.5.8.0", {"start": v(-7, -15.66) * mm, "end": v(-7, -19.66) * mm});
            skLineSegment(sketch, "E4.5.8.1", {"start": v(-3, -15.66) * mm, "end": v(-3, -19.66) * mm});
            skLineSegment(sketch, "E4.5.8.2", {"start": v(-7, -19.66) * mm, "end": v(-3, -19.66) * mm});
            skLineSegment(sketch, "E4.5.8.3", {"start": v(-7, -15.66) * mm, "end": v(-3, -15.66) * mm});
            skLineSegment(sketch, "E4.5.9.0", {"start": v(-7, -21.66) * mm, "end": v(-7, -25.66) * mm});
            skLineSegment(sketch, "E4.5.9.1", {"start": v(-3, -21.66) * mm, "end": v(-3, -25.66) * mm});
            skLineSegment(sketch, "E4.5.9.2", {"start": v(-7, -25.66) * mm, "end": v(-3, -25.66) * mm});
            skLineSegment(sketch, "E4.5.9.3", {"start": v(-7, -21.66) * mm, "end": v(-3, -21.66) * mm});
            skLineSegment(sketch, "E4.5.10.0", {"start": v(-7, -27.66) * mm, "end": v(-7, -31.66) * mm});
            skLineSegment(sketch, "E4.5.10.1", {"start": v(-3, -27.66) * mm, "end": v(-3, -31.66) * mm});
            skLineSegment(sketch, "E4.5.10.2", {"start": v(-7, -31.66) * mm, "end": v(-3, -31.66) * mm});
            skLineSegment(sketch, "E4.5.10.3", {"start": v(-7, -27.66) * mm, "end": v(-3, -27.66) * mm});
            skLineSegment(sketch, "E4.5.11.0", {"start": v(-7, -33.66) * mm, "end": v(-7, -37.66) * mm});
            skLineSegment(sketch, "E4.5.11.1", {"start": v(-3, -33.66) * mm, "end": v(-3, -37.66) * mm});
            skLineSegment(sketch, "E4.5.11.2", {"start": v(-7, -37.66) * mm, "end": v(-3, -37.66) * mm});
            skLineSegment(sketch, "E4.5.11.3", {"start": v(-7, -33.66) * mm, "end": v(-3, -33.66) * mm});
            skLineSegment(sketch, "E4.5.12.0", {"start": v(-7, -39.66) * mm, "end": v(-7, -43.66) * mm});
            skLineSegment(sketch, "E4.5.12.1", {"start": v(-3, -39.66) * mm, "end": v(-3, -43.66) * mm});
            skLineSegment(sketch, "E4.5.12.2", {"start": v(-7, -43.66) * mm, "end": v(-3, -43.66) * mm});
            skLineSegment(sketch, "E4.5.12.3", {"start": v(-7, -39.66) * mm, "end": v(-3, -39.66) * mm});
            skLineSegment(sketch, "E4.5.13.0", {"start": v(-7, -45.66) * mm, "end": v(-7, -49.66) * mm});
            skLineSegment(sketch, "E4.5.13.1", {"start": v(-3, -45.66) * mm, "end": v(-3, -49.66) * mm});
            skLineSegment(sketch, "E4.5.13.2", {"start": v(-7, -49.66) * mm, "end": v(-3, -49.66) * mm});
            skLineSegment(sketch, "E4.5.13.3", {"start": v(-7, -45.66) * mm, "end": v(-3, -45.66) * mm});
            skLineSegment(sketch, "E4.5.14.0", {"start": v(-7, -51.66) * mm, "end": v(-7, -55.66) * mm});
            skLineSegment(sketch, "E4.5.14.1", {"start": v(-3, -51.66) * mm, "end": v(-3, -55.66) * mm});
            skLineSegment(sketch, "E4.5.14.2", {"start": v(-7, -55.66) * mm, "end": v(-3, -55.66) * mm});
            skLineSegment(sketch, "E4.5.14.3", {"start": v(-7, -51.66) * mm, "end": v(-3, -51.66) * mm});
            skLineSegment(sketch, "E4.6.0.0", {"start": v(-1, 32.34) * mm, "end": v(-1, 28.34) * mm});
            skLineSegment(sketch, "E4.6.0.1", {"start": v(3, 32.34) * mm, "end": v(3, 28.34) * mm});
            skLineSegment(sketch, "E4.6.0.2", {"start": v(-1, 28.34) * mm, "end": v(3, 28.34) * mm});
            skLineSegment(sketch, "E4.6.0.3", {"start": v(-1, 32.34) * mm, "end": v(3, 32.34) * mm});
            skLineSegment(sketch, "E4.6.1.0", {"start": v(-1, 26.34) * mm, "end": v(-1, 22.34) * mm});
            skLineSegment(sketch, "E4.6.1.1", {"start": v(3, 26.34) * mm, "end": v(3, 22.34) * mm});
            skLineSegment(sketch, "E4.6.1.2", {"start": v(-1, 22.34) * mm, "end": v(3, 22.34) * mm});
            skLineSegment(sketch, "E4.6.1.3", {"start": v(-1, 26.34) * mm, "end": v(3, 26.34) * mm});
            skLineSegment(sketch, "E4.6.2.0", {"start": v(-1, 20.34) * mm, "end": v(-1, 16.34) * mm});
            skLineSegment(sketch, "E4.6.2.1", {"start": v(3, 20.34) * mm, "end": v(3, 16.34) * mm});
            skLineSegment(sketch, "E4.6.2.2", {"start": v(-1, 16.34) * mm, "end": v(3, 16.34) * mm});
            skLineSegment(sketch, "E4.6.2.3", {"start": v(-1, 20.34) * mm, "end": v(3, 20.34) * mm});
            skLineSegment(sketch, "E4.6.3.0", {"start": v(-1, 14.34) * mm, "end": v(-1, 10.34) * mm});
            skLineSegment(sketch, "E4.6.3.1", {"start": v(3, 14.34) * mm, "end": v(3, 10.34) * mm});
            skLineSegment(sketch, "E4.6.3.2", {"start": v(-1, 10.34) * mm, "end": v(3, 10.34) * mm});
            skLineSegment(sketch, "E4.6.3.3", {"start": v(-1, 14.34) * mm, "end": v(3, 14.34) * mm});
            skLineSegment(sketch, "E4.6.4.0", {"start": v(-1, 8.34) * mm, "end": v(-1, 4.34) * mm});
            skLineSegment(sketch, "E4.6.4.1", {"start": v(3, 8.34) * mm, "end": v(3, 4.34) * mm});
            skLineSegment(sketch, "E4.6.4.2", {"start": v(-1, 4.34) * mm, "end": v(3, 4.34) * mm});
            skLineSegment(sketch, "E4.6.4.3", {"start": v(-1, 8.34) * mm, "end": v(3, 8.34) * mm});
            skLineSegment(sketch, "E4.6.5.0", {"start": v(-1, 2.34) * mm, "end": v(-1, -1.66) * mm});
            skLineSegment(sketch, "E4.6.5.1", {"start": v(3, 2.34) * mm, "end": v(3, -1.66) * mm});
            skLineSegment(sketch, "E4.6.5.2", {"start": v(-1, -1.66) * mm, "end": v(3, -1.66) * mm});
            skLineSegment(sketch, "E4.6.5.3", {"start": v(-1, 2.34) * mm, "end": v(3, 2.34) * mm});
            skLineSegment(sketch, "E4.6.6.0", {"start": v(-1, -3.66) * mm, "end": v(-1, -7.66) * mm});
            skLineSegment(sketch, "E4.6.6.1", {"start": v(3, -3.66) * mm, "end": v(3, -7.66) * mm});
            skLineSegment(sketch, "E4.6.6.2", {"start": v(-1, -7.66) * mm, "end": v(3, -7.66) * mm});
            skLineSegment(sketch, "E4.6.6.3", {"start": v(-1, -3.66) * mm, "end": v(3, -3.66) * mm});
            skLineSegment(sketch, "E4.6.7.0", {"start": v(-1, -9.66) * mm, "end": v(-1, -13.66) * mm});
            skLineSegment(sketch, "E4.6.7.1", {"start": v(3, -9.66) * mm, "end": v(3, -13.66) * mm});
            skLineSegment(sketch, "E4.6.7.2", {"start": v(-1, -13.66) * mm, "end": v(3, -13.66) * mm});
            skLineSegment(sketch, "E4.6.7.3", {"start": v(-1, -9.66) * mm, "end": v(3, -9.66) * mm});
            skLineSegment(sketch, "E4.6.8.0", {"start": v(-1, -15.66) * mm, "end": v(-1, -19.66) * mm});
            skLineSegment(sketch, "E4.6.8.1", {"start": v(3, -15.66) * mm, "end": v(3, -19.66) * mm});
            skLineSegment(sketch, "E4.6.8.2", {"start": v(-1, -19.66) * mm, "end": v(3, -19.66) * mm});
            skLineSegment(sketch, "E4.6.8.3", {"start": v(-1, -15.66) * mm, "end": v(3, -15.66) * mm});
            skLineSegment(sketch, "E4.6.9.0", {"start": v(-1, -21.66) * mm, "end": v(-1, -25.66) * mm});
            skLineSegment(sketch, "E4.6.9.1", {"start": v(3, -21.66) * mm, "end": v(3, -25.66) * mm});
            skLineSegment(sketch, "E4.6.9.2", {"start": v(-1, -25.66) * mm, "end": v(3, -25.66) * mm});
            skLineSegment(sketch, "E4.6.9.3", {"start": v(-1, -21.66) * mm, "end": v(3, -21.66) * mm});
            skLineSegment(sketch, "E4.6.10.0", {"start": v(-1, -27.66) * mm, "end": v(-1, -31.66) * mm});
            skLineSegment(sketch, "E4.6.10.1", {"start": v(3, -27.66) * mm, "end": v(3, -31.66) * mm});
            skLineSegment(sketch, "E4.6.10.2", {"start": v(-1, -31.66) * mm, "end": v(3, -31.66) * mm});
            skLineSegment(sketch, "E4.6.10.3", {"start": v(-1, -27.66) * mm, "end": v(3, -27.66) * mm});
            skLineSegment(sketch, "E4.6.11.0", {"start": v(-1, -33.66) * mm, "end": v(-1, -37.66) * mm});
            skLineSegment(sketch, "E4.6.11.1", {"start": v(3, -33.66) * mm, "end": v(3, -37.66) * mm});
            skLineSegment(sketch, "E4.6.11.2", {"start": v(-1, -37.66) * mm, "end": v(3, -37.66) * mm});
            skLineSegment(sketch, "E4.6.11.3", {"start": v(-1, -33.66) * mm, "end": v(3, -33.66) * mm});
            skLineSegment(sketch, "E4.6.12.0", {"start": v(-1, -39.66) * mm, "end": v(-1, -43.66) * mm});
            skLineSegment(sketch, "E4.6.12.1", {"start": v(3, -39.66) * mm, "end": v(3, -43.66) * mm});
            skLineSegment(sketch, "E4.6.12.2", {"start": v(-1, -43.66) * mm, "end": v(3, -43.66) * mm});
            skLineSegment(sketch, "E4.6.12.3", {"start": v(-1, -39.66) * mm, "end": v(3, -39.66) * mm});
            skLineSegment(sketch, "E4.6.13.0", {"start": v(-1, -45.66) * mm, "end": v(-1, -49.66) * mm});
            skLineSegment(sketch, "E4.6.13.1", {"start": v(3, -45.66) * mm, "end": v(3, -49.66) * mm});
            skLineSegment(sketch, "E4.6.13.2", {"start": v(-1, -49.66) * mm, "end": v(3, -49.66) * mm});
            skLineSegment(sketch, "E4.6.13.3", {"start": v(-1, -45.66) * mm, "end": v(3, -45.66) * mm});
            skLineSegment(sketch, "E4.6.14.0", {"start": v(-1, -51.66) * mm, "end": v(-1, -55.66) * mm});
            skLineSegment(sketch, "E4.6.14.1", {"start": v(3, -51.66) * mm, "end": v(3, -55.66) * mm});
            skLineSegment(sketch, "E4.6.14.2", {"start": v(-1, -55.66) * mm, "end": v(3, -55.66) * mm});
            skLineSegment(sketch, "E4.6.14.3", {"start": v(-1, -51.66) * mm, "end": v(3, -51.66) * mm});
            skLineSegment(sketch, "E4.7.0.0", {"start": v(5, 32.34) * mm, "end": v(5, 28.34) * mm});
            skLineSegment(sketch, "E4.7.0.1", {"start": v(9, 32.34) * mm, "end": v(9, 28.34) * mm});
            skLineSegment(sketch, "E4.7.0.2", {"start": v(5, 28.34) * mm, "end": v(9, 28.34) * mm});
            skLineSegment(sketch, "E4.7.0.3", {"start": v(5, 32.34) * mm, "end": v(9, 32.34) * mm});
            skLineSegment(sketch, "E4.7.1.0", {"start": v(5, 26.34) * mm, "end": v(5, 22.34) * mm});
            skLineSegment(sketch, "E4.7.1.1", {"start": v(9, 26.34) * mm, "end": v(9, 22.34) * mm});
            skLineSegment(sketch, "E4.7.1.2", {"start": v(5, 22.34) * mm, "end": v(9, 22.34) * mm});
            skLineSegment(sketch, "E4.7.1.3", {"start": v(5, 26.34) * mm, "end": v(9, 26.34) * mm});
            skLineSegment(sketch, "E4.7.2.0", {"start": v(5, 20.34) * mm, "end": v(5, 16.34) * mm});
            skLineSegment(sketch, "E4.7.2.1", {"start": v(9, 20.34) * mm, "end": v(9, 16.34) * mm});
            skLineSegment(sketch, "E4.7.2.2", {"start": v(5, 16.34) * mm, "end": v(9, 16.34) * mm});
            skLineSegment(sketch, "E4.7.2.3", {"start": v(5, 20.34) * mm, "end": v(9, 20.34) * mm});
            skLineSegment(sketch, "E4.7.3.0", {"start": v(5, 14.34) * mm, "end": v(5, 10.34) * mm});
            skLineSegment(sketch, "E4.7.3.1", {"start": v(9, 14.34) * mm, "end": v(9, 10.34) * mm});
            skLineSegment(sketch, "E4.7.3.2", {"start": v(5, 10.34) * mm, "end": v(9, 10.34) * mm});
            skLineSegment(sketch, "E4.7.3.3", {"start": v(5, 14.34) * mm, "end": v(9, 14.34) * mm});
            skLineSegment(sketch, "E4.7.4.0", {"start": v(5, 8.34) * mm, "end": v(5, 4.34) * mm});
            skLineSegment(sketch, "E4.7.4.1", {"start": v(9, 8.34) * mm, "end": v(9, 4.34) * mm});
            skLineSegment(sketch, "E4.7.4.2", {"start": v(5, 4.34) * mm, "end": v(9, 4.34) * mm});
            skLineSegment(sketch, "E4.7.4.3", {"start": v(5, 8.34) * mm, "end": v(9, 8.34) * mm});
            skLineSegment(sketch, "E4.7.5.0", {"start": v(5, 2.34) * mm, "end": v(5, -1.66) * mm});
            skLineSegment(sketch, "E4.7.5.1", {"start": v(9, 2.34) * mm, "end": v(9, -1.66) * mm});
            skLineSegment(sketch, "E4.7.5.2", {"start": v(5, -1.66) * mm, "end": v(9, -1.66) * mm});
            skLineSegment(sketch, "E4.7.5.3", {"start": v(5, 2.34) * mm, "end": v(9, 2.34) * mm});
            skLineSegment(sketch, "E4.7.6.0", {"start": v(5, -3.66) * mm, "end": v(5, -7.66) * mm});
            skLineSegment(sketch, "E4.7.6.1", {"start": v(9, -3.66) * mm, "end": v(9, -7.66) * mm});
            skLineSegment(sketch, "E4.7.6.2", {"start": v(5, -7.66) * mm, "end": v(9, -7.66) * mm});
            skLineSegment(sketch, "E4.7.6.3", {"start": v(5, -3.66) * mm, "end": v(9, -3.66) * mm});
            skLineSegment(sketch, "E4.7.7.0", {"start": v(5, -9.66) * mm, "end": v(5, -13.66) * mm});
            skLineSegment(sketch, "E4.7.7.1", {"start": v(9, -9.66) * mm, "end": v(9, -13.66) * mm});
            skLineSegment(sketch, "E4.7.7.2", {"start": v(5, -13.66) * mm, "end": v(9, -13.66) * mm});
            skLineSegment(sketch, "E4.7.7.3", {"start": v(5, -9.66) * mm, "end": v(9, -9.66) * mm});
            skLineSegment(sketch, "E4.7.8.0", {"start": v(5, -15.66) * mm, "end": v(5, -19.66) * mm});
            skLineSegment(sketch, "E4.7.8.1", {"start": v(9, -15.66) * mm, "end": v(9, -19.66) * mm});
            skLineSegment(sketch, "E4.7.8.2", {"start": v(5, -19.66) * mm, "end": v(9, -19.66) * mm});
            skLineSegment(sketch, "E4.7.8.3", {"start": v(5, -15.66) * mm, "end": v(9, -15.66) * mm});
            skLineSegment(sketch, "E4.7.9.0", {"start": v(5, -21.66) * mm, "end": v(5, -25.66) * mm});
            skLineSegment(sketch, "E4.7.9.1", {"start": v(9, -21.66) * mm, "end": v(9, -25.66) * mm});
            skLineSegment(sketch, "E4.7.9.2", {"start": v(5, -25.66) * mm, "end": v(9, -25.66) * mm});
            skLineSegment(sketch, "E4.7.9.3", {"start": v(5, -21.66) * mm, "end": v(9, -21.66) * mm});
            skLineSegment(sketch, "E4.7.10.0", {"start": v(5, -27.66) * mm, "end": v(5, -31.66) * mm});
            skLineSegment(sketch, "E4.7.10.1", {"start": v(9, -27.66) * mm, "end": v(9, -31.66) * mm});
            skLineSegment(sketch, "E4.7.10.2", {"start": v(5, -31.66) * mm, "end": v(9, -31.66) * mm});
            skLineSegment(sketch, "E4.7.10.3", {"start": v(5, -27.66) * mm, "end": v(9, -27.66) * mm});
            skLineSegment(sketch, "E4.7.11.0", {"start": v(5, -33.66) * mm, "end": v(5, -37.66) * mm});
            skLineSegment(sketch, "E4.7.11.1", {"start": v(9, -33.66) * mm, "end": v(9, -37.66) * mm});
            skLineSegment(sketch, "E4.7.11.2", {"start": v(5, -37.66) * mm, "end": v(9, -37.66) * mm});
            skLineSegment(sketch, "E4.7.11.3", {"start": v(5, -33.66) * mm, "end": v(9, -33.66) * mm});
            skLineSegment(sketch, "E4.7.12.0", {"start": v(5, -39.66) * mm, "end": v(5, -43.66) * mm});
            skLineSegment(sketch, "E4.7.12.1", {"start": v(9, -39.66) * mm, "end": v(9, -43.66) * mm});
            skLineSegment(sketch, "E4.7.12.2", {"start": v(5, -43.66) * mm, "end": v(9, -43.66) * mm});
            skLineSegment(sketch, "E4.7.12.3", {"start": v(5, -39.66) * mm, "end": v(9, -39.66) * mm});
            skLineSegment(sketch, "E4.7.13.0", {"start": v(5, -45.66) * mm, "end": v(5, -49.66) * mm});
            skLineSegment(sketch, "E4.7.13.1", {"start": v(9, -45.66) * mm, "end": v(9, -49.66) * mm});
            skLineSegment(sketch, "E4.7.13.2", {"start": v(5, -49.66) * mm, "end": v(9, -49.66) * mm});
            skLineSegment(sketch, "E4.7.13.3", {"start": v(5, -45.66) * mm, "end": v(9, -45.66) * mm});
            skLineSegment(sketch, "E4.7.14.0", {"start": v(5, -51.66) * mm, "end": v(5, -55.66) * mm});
            skLineSegment(sketch, "E4.7.14.1", {"start": v(9, -51.66) * mm, "end": v(9, -55.66) * mm});
            skLineSegment(sketch, "E4.7.14.2", {"start": v(5, -55.66) * mm, "end": v(9, -55.66) * mm});
            skLineSegment(sketch, "E4.7.14.3", {"start": v(5, -51.66) * mm, "end": v(9, -51.66) * mm});
            skLineSegment(sketch, "E4.direction1", {"start": v(-37, 28.34) * mm, "end": v(-31, 28.34) * mm, "construction": true});
            skLineSegment(sketch, "E4.direction2", {"start": v(-37, 28.34) * mm, "end": v(-37, 22.34) * mm, "construction": true});
            skSolve(sketch);
        }
        {
            var Q0;
            Q0 = qSketchRegion(id + "F2", true);
            extrude(context, id + "F3", {"entities" : qUnion([Q0]), "operationType" : NewBodyOperationType.REMOVE, "oppositeDirection" : true, "depth" : .5 * mm});
        }
        {
            var Q0;
            Q0=makeQuery(id+"F1.opExtrude","SWEPT_FACE",FACE,{"disambiguationData":[OSD([sQuery(id+"F0.wireOp",EDGE,"E2.right")])]});
            var sketch = newSketch(context, id + "F4", { "sketchPlane" : qUnion([Q0])});
            skCircle(sketch, "E5", {"center": v(-63.16, 1) * mm, "radius": 0.5 * mm});
            skSolve(sketch);
        }
        {
            var Q0;
            Q0 = qSketchRegion(id + "F4", true);
            extrude(context, id + "F5", {"entities" : qUnion([Q0]), "operationType" : NewBodyOperationType.REMOVE, "endBound" : BoundingType.UP_TO_NEXT, "oppositeDirection" : true, "depth" : 25 * mm});
        }
        {
            var Q0;
            Q0=makeQuery(id+"F1.opExtrude","CAP_FACE",FACE,{"disambiguationData":[OSD([sQuery(id+"F0.wireOp",EDGE,"E0.bottom"),sQuery(id+"F0.wireOp",EDGE,"E0.top"),sQuery(id+"F0.wireOp",EDGE,"E0.left"),sQuery(id+"F0.wireOp",EDGE,"E0.right"),sQuery(id+"F0.wireOp",EDGE,"E1.top"),sQuery(id+"F0.wireOp",EDGE,"E1.right"),sQuery(id+"F0.wireOp",EDGE,"E2.top"),sQuery(id+"F0.wireOp",EDGE,"E2.right")])],"isStart":true});
            var sketch = newSketch(context, id + "F6", { "sketchPlane" : qUnion([Q0])});
            skCircle(sketch, "E6", {"center": v(-14, 15.66) * mm, "radius": 7 * mm});
            skLineSegment(sketch, "E7.bottom", {"start": v(-28, -23.34) * mm, "end": v(-35, -23.34) * mm});
            skLineSegment(sketch, "E7.top", {"start": v(-28, -30.34) * mm, "end": v(-35, -30.34) * mm});
            skLineSegment(sketch, "E7.left", {"start": v(-28, -23.34) * mm, "end": v(-28, -30.34) * mm});
            skLineSegment(sketch, "E7.right", {"start": v(-35, -23.34) * mm, "end": v(-35, -30.34) * mm});
            skLineSegment(sketch, "E8.bottom", {"start": v(0, -23.34) * mm, "end": v(7, -23.34) * mm});
            skLineSegment(sketch, "E8.top", {"start": v(0, -30.34) * mm, "end": v(7, -30.34) * mm});
            skLineSegment(sketch, "E8.left", {"start": v(0, -23.34) * mm, "end": v(0, -30.34) * mm});
            skLineSegment(sketch, "E8.right", {"start": v(7, -23.34) * mm, "end": v(7, -30.34) * mm});
            skSolve(sketch);
        }
        {
            var Q0;
            Q0 = qSketchRegion(id + "F6", true);
            extrude(context, id + "F7", {"entities" : qUnion([Q0]), "operationType" : NewBodyOperationType.REMOVE, "oppositeDirection" : true, "depth" : 1.2 * mm});
        }
    });
